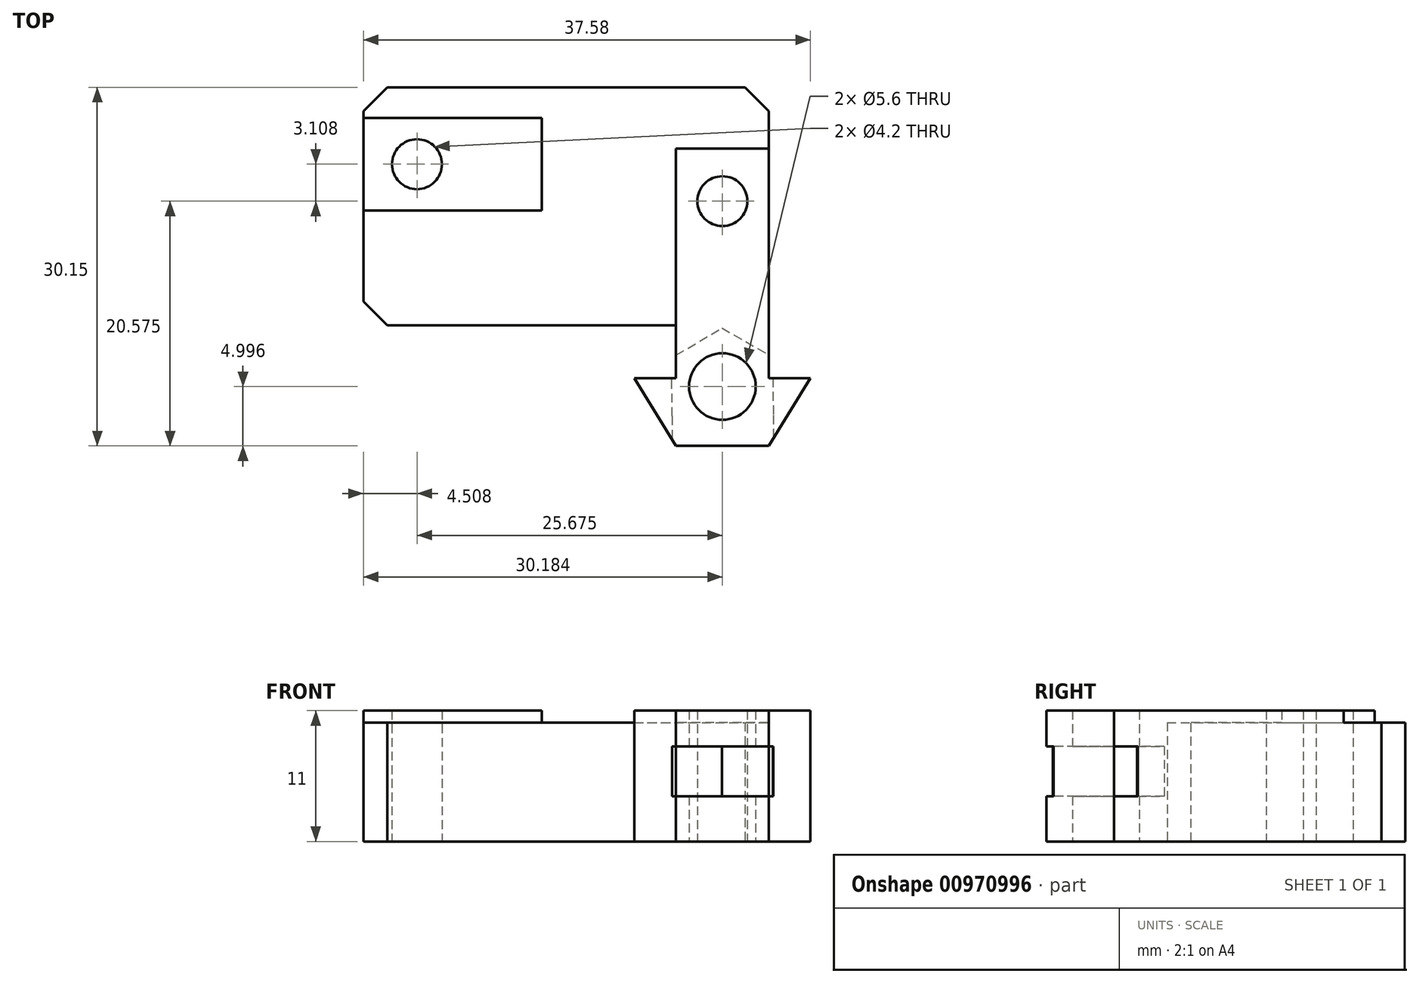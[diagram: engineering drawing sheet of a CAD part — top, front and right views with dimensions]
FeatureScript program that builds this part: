
annotation { "Feature Type Name" : "Feature", "Feature Type Description" : "" }
export const myFeature = defineFeature(function(context is Context, id is Id, definition is map)
    precondition{}
    {
        {
            var Q0;
            Q0=qCreatedBy(makeId("Top.planeOp"),FACE);
            var sketch = newSketch(context, id + "F0", { "sketchPlane" : qUnion([Q0])});
            skLineSegment(sketch, "E0.bottom", {"start": v(7.44, 6.9) * mm, "end": v(15.24, 6.9) * mm});
            skLineSegment(sketch, "E0.top", {"start": v(7.44, -18.1) * mm, "end": v(15.24, -18.1) * mm});
            skLineSegment(sketch, "E0.left", {"start": v(7.44, 6.9) * mm, "end": v(7.44, -18.1) * mm});
            skLineSegment(sketch, "E0.right", {"start": v(15.24, 6.9) * mm, "end": v(15.24, -18.1) * mm});
            skLineSegment(sketch, "E1.bottom", {"start": v(-18.84, 9.5) * mm, "end": v(-3.84, 9.5) * mm});
            skLineSegment(sketch, "E1.top", {"start": v(-18.84, 1.7) * mm, "end": v(-3.84, 1.7) * mm});
            skLineSegment(sketch, "E1.left", {"start": v(-18.84, 9.5) * mm, "end": v(-18.84, 1.7) * mm});
            skLineSegment(sketch, "E1.right", {"start": v(-3.84, 9.5) * mm, "end": v(-3.84, 1.7) * mm});
            skLineSegment(sketch, "E2", {"start": v(-18.84, 5.6) * mm, "end": v(-3.84, 5.6) * mm, "construction": true});
            skLineSegment(sketch, "E3", {"start": v(11.34, -18.1) * mm, "end": v(11.34, 6.9) * mm, "construction": true});
            skLineSegment(sketch, "E4", {"start": v(11.34, 6.9) * mm, "end": v(11.34, -13.1) * mm, "construction": true});
            skCircle(sketch, "E5.cCircle", {"center": v(11.34, -13.1) * mm, "radius": 4.25 * mm, "construction": true});
            skLineSegment(sketch, "E5.0", {"start": v(15.61, -15.51) * mm, "end": v(11.39, -18) * mm});
            skLineSegment(sketch, "E5.1", {"start": v(11.39, -18) * mm, "end": v(7.12, -15.58) * mm});
            skLineSegment(sketch, "E5.2", {"start": v(7.12, -15.58) * mm, "end": v(7.07, -10.68) * mm});
            skLineSegment(sketch, "E5.3", {"start": v(7.07, -10.68) * mm, "end": v(11.3, -8.19) * mm});
            skLineSegment(sketch, "E5.4", {"start": v(11.3, -8.19) * mm, "end": v(15.57, -10.6) * mm});
            skLineSegment(sketch, "E5.5", {"start": v(15.57, -10.6) * mm, "end": v(15.61, -15.51) * mm});
            skPoint(sketch, "E5.0.midPoint", {"position": v(13.5, -16.76) * mm});
            skCircle(sketch, "E6", {"center": v(11.34, -13.1) * mm, "radius": 2.8 * mm});
            skCircle(sketch, "E7", {"center": v(11.34, 2.49) * mm, "radius": 2.1 * mm});
            skCircle(sketch, "E8", {"center": v(-14.33, 5.6) * mm, "radius": 2.1 * mm});
            skLineSegment(sketch, "E9", {"start": v(15.24, -18.1) * mm, "end": v(15.24, -12.4) * mm, "construction": true});
            skLineSegment(sketch, "E10", {"start": v(15.24, -12.4) * mm, "end": v(18.74, -12.4) * mm});
            skLineSegment(sketch, "E11.MirrorCS", {"start": v(7.44, -12.4) * mm, "end": v(3.94, -12.4) * mm});
            skLineSegment(sketch, "E12", {"start": v(18.74, -12.4) * mm, "end": v(15.24, -18.1) * mm});
            skLineSegment(sketch, "E13", {"start": v(3.94, -12.4) * mm, "end": v(7.44, -18.1) * mm});
            skPoint(sketch, "E14.end.orphan", {"position": v(15.24, -18.1) * mm});
            skPoint(sketch, "E14.start.orphan", {"position": v(18.8, -18.1) * mm});
            skPoint(sketch, "E15.MirrorCS.end.orphan", {"position": v(7.44, -18.1) * mm});
            skPoint(sketch, "E15.MirrorCS.start.orphan", {"position": v(3.9, -18.1) * mm});
            skPoint(sketch, "E16.MirrorCS.start.orphan", {"position": v(3.94, -12.4) * mm});
            skLineSegment(sketch, "E17.bottom", {"start": v(-18.84, 12.06) * mm, "end": v(15.24, 12.06) * mm});
            skLineSegment(sketch, "E17.top", {"start": v(-18.84, -7.94) * mm, "end": v(15.24, -7.94) * mm});
            skLineSegment(sketch, "E17.left", {"start": v(-18.84, 12.06) * mm, "end": v(-18.84, -7.94) * mm});
            skLineSegment(sketch, "E17.right", {"start": v(15.24, 12.06) * mm, "end": v(15.24, -7.94) * mm});
            skLineSegment(sketch, "E18", {"start": v(5.5, -7.94) * mm, "end": v(5.5, -12.4) * mm, "construction": true});
            skLineSegment(sketch, "E19", {"start": v(15.61, -15.51) * mm, "end": v(15.61, -17.49) * mm});
            skLineSegment(sketch, "E20", {"start": v(7.12, -15.58) * mm, "end": v(7.12, -17.56) * mm});
            skSolve(sketch);
        }
        {
            var Q0;
            {var subQ2=sQuery(id+"F0.wireOp",EDGE,"E0.bottom");Q0=makeQuery(id+"F0.imprint","IMPRINT",FACE,{"disambiguationData":[TD([[makeQuery(id+"F0.imprint","IMPRINT",EDGE,{"derivedFrom":subQ2}),1.0]])]});}
            var Q1;
            {var subQ0=sQuery(id+"F0.wireOp",EDGE,"E5.3");var subQ1=sQuery(id+"F0.wireOp",EDGE,"E0.left");var subQ2=makeQuery(id+"F0.imprint","INTERSECT",VERTEX,{"derivedFrom":[subQ1,subQ0]});Q1=makeQuery(id+"F0.imprint","IMPRINT",FACE,{"disambiguationData":[TD([[makeQuery(id+"F0.imprint","IMPRINT",EDGE,{"disambiguationData":[TD([[subQ2,1.0]])],"derivedFrom":subQ1}),1.0]])]});}
            var Q2;
            {var subQ5=sQuery(id+"F0.wireOp",EDGE,"E20");var subQ9=makeQuery(id+"F0.imprint","IMPRINT",EDGE,{"derivedFrom":subQ5});Q2=qUnion([makeQuery(id+"F0.imprint","IMPRINT",FACE,{"disambiguationData":[TD([[subQ9,-1.0]])]}),makeQuery(id+"F0.imprint","IMPRINT",FACE,{"disambiguationData":[TD([[subQ9,1.0]])]})]);}
            var Q3;
            {var subQ5=sQuery(id+"F0.wireOp",EDGE,"E19");var subQ6=makeQuery(id+"F0.imprint","IMPRINT",EDGE,{"derivedFrom":subQ5});Q3=qUnion([makeQuery(id+"F0.imprint","IMPRINT",FACE,{"disambiguationData":[TD([[subQ6,1.0]])]}),makeQuery(id+"F0.imprint","IMPRINT",FACE,{"disambiguationData":[TD([[subQ6,-1.0]])]})]);}
            var Q4;
            Q4=makeQuery(id+"F0.imprint","IMPRINT",FACE,{"disambiguationData":[TD([[makeQuery(id+"F0.imprint","IMPRINT",EDGE,{"derivedFrom":sQuery(id+"F0.wireOp",EDGE,"E1.bottom")}),-1.0]])]});
            var Q5;
            {var subQ1=sQuery(id+"F0.wireOp",EDGE,"E0.bottom");Q5=makeQuery(id+"F0.imprint","IMPRINT",FACE,{"disambiguationData":[TD([[makeQuery(id+"F0.imprint","IMPRINT",EDGE,{"derivedFrom":subQ1}),-1.0]])]});}
            var Q6;
            {var subQ1=sQuery(id+"F0.wireOp",EDGE,"E0.top");Q6=makeQuery(id+"F0.imprint","IMPRINT",FACE,{"disambiguationData":[TD([[makeQuery(id+"F0.imprint","IMPRINT",EDGE,{"derivedFrom":subQ1}),1.0]])]});}
            var Q7;
            {var subQ0=sQuery(id+"F0.wireOp",EDGE,"E11.MirrorCS");var subQ1=sQuery(id+"F0.wireOp",EDGE,"E0.left");var subQ2=makeQuery(id+"F0.imprint","INTERSECT",VERTEX,{"derivedFrom":[subQ1,subQ0]});Q7=makeQuery(id+"F0.imprint","IMPRINT",FACE,{"disambiguationData":[TD([[makeQuery(id+"F0.imprint","IMPRINT",EDGE,{"disambiguationData":[TD([[subQ2,-1.0]])],"derivedFrom":subQ1}),-1.0]])]});}
            var Q8;
            {var subQ0=sQuery(id+"F0.wireOp",EDGE,"E10");var subQ1=sQuery(id+"F0.wireOp",EDGE,"E0.right");var subQ2=makeQuery(id+"F0.imprint","INTERSECT",VERTEX,{"derivedFrom":[subQ1,subQ0]});Q8=makeQuery(id+"F0.imprint","IMPRINT",FACE,{"disambiguationData":[TD([[makeQuery(id+"F0.imprint","IMPRINT",EDGE,{"disambiguationData":[TD([[subQ2,-1.0]])],"derivedFrom":subQ1}),1.0]])]});}
            var Q9;
            Q9=makeQuery(id+"F0.imprint","IMPRINT",FACE,{"disambiguationData":[TD([[makeQuery(id+"F0.imprint","IMPRINT",EDGE,{"derivedFrom":sQuery(id+"F0.wireOp",EDGE,"E6")}),-1.0]])]});
            extrude(context, id + "F1", {"entities" : qUnion([Q0, Q1, Q2, Q3, Q4, Q5, Q6, Q7, Q8, Q9]), "depth" : 10 * mm, "offsetDistance" : 25 * mm});
        }
        {
            var Q0;
            Q0=makeQuery(id+"F0.imprint","IMPRINT",FACE,{"disambiguationData":[TD([[makeQuery(id+"F0.imprint","IMPRINT",EDGE,{"derivedFrom":sQuery(id+"F0.wireOp",EDGE,"E1.bottom")}),-1.0]])]});
            var Q1;
            {var subQ1=sQuery(id+"F0.wireOp",EDGE,"E0.bottom");Q1=makeQuery(id+"F0.imprint","IMPRINT",FACE,{"disambiguationData":[TD([[makeQuery(id+"F0.imprint","IMPRINT",EDGE,{"derivedFrom":subQ1}),-1.0]])]});}
            var Q2;
            {var subQ0=sQuery(id+"F0.wireOp",EDGE,"E11.MirrorCS");var subQ1=sQuery(id+"F0.wireOp",EDGE,"E0.left");var subQ2=makeQuery(id+"F0.imprint","INTERSECT",VERTEX,{"derivedFrom":[subQ1,subQ0]});Q2=makeQuery(id+"F0.imprint","IMPRINT",FACE,{"disambiguationData":[TD([[makeQuery(id+"F0.imprint","IMPRINT",EDGE,{"disambiguationData":[TD([[subQ2,-1.0]])],"derivedFrom":subQ1}),-1.0]])]});}
            var Q3;
            {var subQ5=sQuery(id+"F0.wireOp",EDGE,"E20");Q3=makeQuery(id+"F0.imprint","IMPRINT",FACE,{"disambiguationData":[TD([[makeQuery(id+"F0.imprint","IMPRINT",EDGE,{"derivedFrom":subQ5}),1.0]])]});}
            var Q4;
            {var subQ1=sQuery(id+"F0.wireOp",EDGE,"E0.top");Q4=makeQuery(id+"F0.imprint","IMPRINT",FACE,{"disambiguationData":[TD([[makeQuery(id+"F0.imprint","IMPRINT",EDGE,{"derivedFrom":subQ1}),1.0]])]});}
            var Q5;
            {var subQ3=sQuery(id+"F0.wireOp",EDGE,"E19");Q5=makeQuery(id+"F0.imprint","IMPRINT",FACE,{"disambiguationData":[TD([[makeQuery(id+"F0.imprint","IMPRINT",EDGE,{"derivedFrom":subQ3}),1.0]])]});}
            var Q6;
            {var subQ5=sQuery(id+"F0.wireOp",EDGE,"E19");Q6=makeQuery(id+"F0.imprint","IMPRINT",FACE,{"disambiguationData":[TD([[makeQuery(id+"F0.imprint","IMPRINT",EDGE,{"derivedFrom":subQ5}),-1.0]])]});}
            var Q7;
            {var subQ0=sQuery(id+"F0.wireOp",EDGE,"E20");Q7=makeQuery(id+"F0.imprint","IMPRINT",FACE,{"disambiguationData":[TD([[makeQuery(id+"F0.imprint","IMPRINT",EDGE,{"derivedFrom":subQ0}),-1.0]])]});}
            var Q8;
            Q8=makeQuery(id+"F0.imprint","IMPRINT",FACE,{"disambiguationData":[TD([[makeQuery(id+"F0.imprint","IMPRINT",EDGE,{"derivedFrom":sQuery(id+"F0.wireOp",EDGE,"E6")}),-1.0]])]});
            var Q9;
            {var subQ0=sQuery(id+"F0.wireOp",EDGE,"E5.3");var subQ1=sQuery(id+"F0.wireOp",EDGE,"E0.left");var subQ2=makeQuery(id+"F0.imprint","INTERSECT",VERTEX,{"derivedFrom":[subQ1,subQ0]});Q9=makeQuery(id+"F0.imprint","IMPRINT",FACE,{"disambiguationData":[TD([[makeQuery(id+"F0.imprint","IMPRINT",EDGE,{"disambiguationData":[TD([[subQ2,1.0]])],"derivedFrom":subQ1}),1.0]])]});}
            var Q10;
            {var subQ0=sQuery(id+"F0.wireOp",EDGE,"E10");var subQ1=sQuery(id+"F0.wireOp",EDGE,"E0.right");var subQ2=makeQuery(id+"F0.imprint","INTERSECT",VERTEX,{"derivedFrom":[subQ1,subQ0]});Q10=makeQuery(id+"F0.imprint","IMPRINT",FACE,{"disambiguationData":[TD([[makeQuery(id+"F0.imprint","IMPRINT",EDGE,{"disambiguationData":[TD([[subQ2,-1.0]])],"derivedFrom":subQ1}),1.0]])]});}
            extrude(context, id + "F2", {"entities" : qUnion([Q0, Q1, Q2, Q3, Q4, Q5, Q6, Q7, Q8, Q9, Q10]), "operationType" : NewBodyOperationType.ADD, "depth" : 11 * mm, "offsetDistance" : 25 * mm, "hasSecondDirection" : true, "secondDirectionOppositeDirection" : false, "secondDirectionDepth" : 9 * mm});
        }
        {
            var Q0;
            {var subQ0=sQuery(id+"F0.wireOp",EDGE,"E10");var subQ1=sQuery(id+"F0.wireOp",EDGE,"E0.right");var subQ2=makeQuery(id+"F0.imprint","INTERSECT",VERTEX,{"derivedFrom":[subQ1,subQ0]});Q0=makeQuery(id+"F0.imprint","IMPRINT",FACE,{"disambiguationData":[TD([[makeQuery(id+"F0.imprint","IMPRINT",EDGE,{"disambiguationData":[TD([[subQ2,1.0]])],"derivedFrom":subQ1}),1.0]])]});}
            var Q1;
            Q1=makeQuery(id+"F0.imprint","IMPRINT",FACE,{"disambiguationData":[TD([[makeQuery(id+"F0.imprint","IMPRINT",EDGE,{"derivedFrom":sQuery(id+"F0.wireOp",EDGE,"E6")}),-1.0]])]});
            var Q2;
            {var subQ0=sQuery(id+"F0.wireOp",EDGE,"E10");var subQ1=sQuery(id+"F0.wireOp",EDGE,"E0.right");var subQ2=makeQuery(id+"F0.imprint","INTERSECT",VERTEX,{"derivedFrom":[subQ1,subQ0]});Q2=makeQuery(id+"F0.imprint","IMPRINT",FACE,{"disambiguationData":[TD([[makeQuery(id+"F0.imprint","IMPRINT",EDGE,{"disambiguationData":[TD([[subQ2,-1.0]])],"derivedFrom":subQ1}),1.0]])]});}
            var Q3;
            {var subQ0=sQuery(id+"F0.wireOp",EDGE,"E11.MirrorCS");var subQ1=sQuery(id+"F0.wireOp",EDGE,"E0.left");var subQ2=makeQuery(id+"F0.imprint","INTERSECT",VERTEX,{"derivedFrom":[subQ1,subQ0]});Q3=makeQuery(id+"F0.imprint","IMPRINT",FACE,{"disambiguationData":[TD([[makeQuery(id+"F0.imprint","IMPRINT",EDGE,{"disambiguationData":[TD([[subQ2,-1.0]])],"derivedFrom":subQ1}),-1.0]])]});}
            var Q4;
            {var subQ0=sQuery(id+"F0.wireOp",EDGE,"E11.MirrorCS");var subQ1=sQuery(id+"F0.wireOp",EDGE,"E0.left");var subQ2=makeQuery(id+"F0.imprint","INTERSECT",VERTEX,{"derivedFrom":[subQ1,subQ0]});Q4=makeQuery(id+"F0.imprint","IMPRINT",FACE,{"disambiguationData":[TD([[makeQuery(id+"F0.imprint","IMPRINT",EDGE,{"disambiguationData":[TD([[subQ2,1.0]])],"derivedFrom":subQ1}),-1.0]])]});}
            var Q5;
            {var subQ1=sQuery(id+"F0.wireOp",EDGE,"E0.top");Q5=makeQuery(id+"F0.imprint","IMPRINT",FACE,{"disambiguationData":[TD([[makeQuery(id+"F0.imprint","IMPRINT",EDGE,{"derivedFrom":subQ1}),1.0]])]});}
            var Q6;
            {var subQ5=sQuery(id+"F0.wireOp",EDGE,"E19");Q6=makeQuery(id+"F0.imprint","IMPRINT",FACE,{"disambiguationData":[TD([[makeQuery(id+"F0.imprint","IMPRINT",EDGE,{"derivedFrom":subQ5}),-1.0]])]});}
            var Q7;
            {var subQ5=sQuery(id+"F0.wireOp",EDGE,"E20");Q7=makeQuery(id+"F0.imprint","IMPRINT",FACE,{"disambiguationData":[TD([[makeQuery(id+"F0.imprint","IMPRINT",EDGE,{"derivedFrom":subQ5}),1.0]])]});}
            extrude(context, id + "F3", {"entities" : qUnion([Q0, Q1, Q2, Q3, Q4, Q5, Q6, Q7]), "operationType" : NewBodyOperationType.REMOVE, "depth" : 8 * mm, "offsetDistance" : 25 * mm, "hasSecondDirection" : true, "secondDirectionOppositeDirection" : false, "secondDirectionDepth" : 3.8 * mm});
        }
        {
            var Q0;
            Q0=makeQuery(id+"F1.opExtrude","SWEPT_EDGE",EDGE,{"disambiguationData":[OSD([sQuery(id+"F0.wireOp",EDGE,"E17.bottom"),sQuery(id+"F0.wireOp",EDGE,"E17.right")])]});
            var Q1;
            Q1=makeQuery(id+"F1.opExtrude","SWEPT_EDGE",EDGE,{"disambiguationData":[OSD([sQuery(id+"F0.wireOp",EDGE,"E17.top"),sQuery(id+"F0.wireOp",EDGE,"E17.left")])]});
            var Q2;
            Q2=makeQuery(id+"F1.opExtrude","SWEPT_EDGE",EDGE,{"disambiguationData":[OSD([sQuery(id+"F0.wireOp",EDGE,"E17.bottom"),sQuery(id+"F0.wireOp",EDGE,"E17.left")])]});
            chamfer(context, id + "F4", {"entities" : qUnion([Q0, Q1, Q2]), "width" : 2 * mm, "tangentPropagation" : true});
        }
    });
